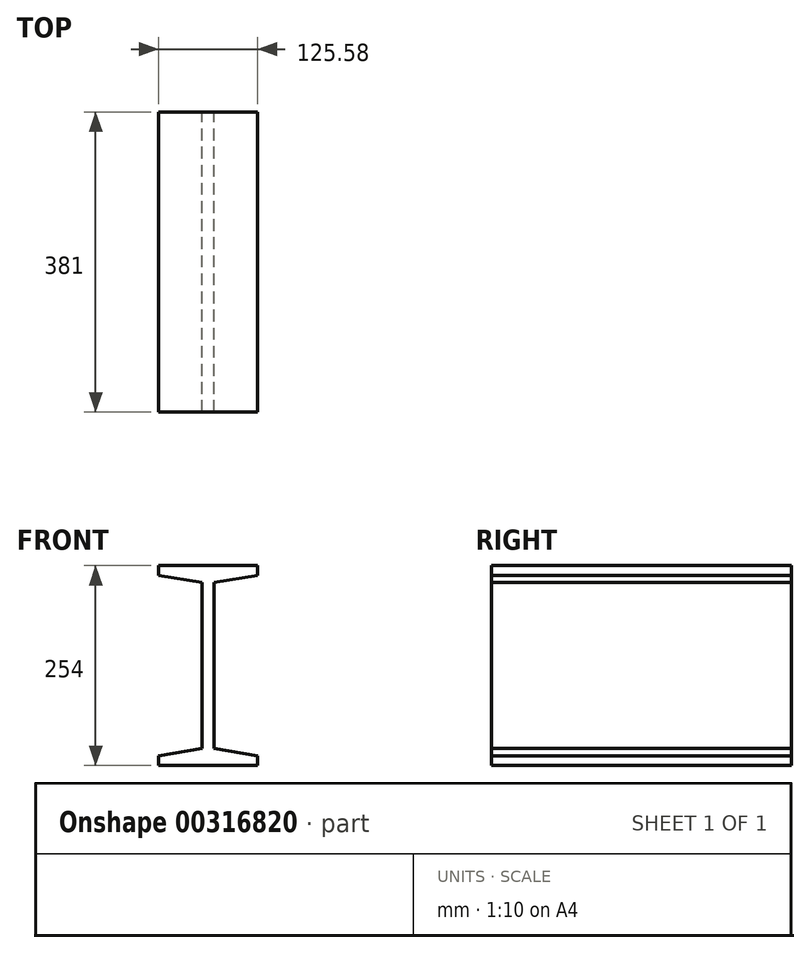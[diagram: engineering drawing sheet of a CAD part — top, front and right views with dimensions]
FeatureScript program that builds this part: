
annotation { "Feature Type Name" : "Feature", "Feature Type Description" : "" }
export const myFeature = defineFeature(function(context is Context, id is Id, definition is map)
    precondition{}
    {
        {
            var Q0;
            Q0=qCreatedBy(makeId("Front.planeOp"),FACE);
            var sketch = newSketch(context, id + "F0", { "sketchPlane" : qUnion([Q0])});
            skLineSegment(sketch, "E0", {"start": v(-62.79, 127) * mm, "end": v(62.79, 127) * mm});
            skLineSegment(sketch, "E1", {"start": v(62.79, 127) * mm, "end": v(62.79, 114.53) * mm});
            skLineSegment(sketch, "E2", {"start": v(-62.79, 127) * mm, "end": v(-62.79, 114.53) * mm});
            skLineSegment(sketch, "E3", {"start": v(-62.79, 114.53) * mm, "end": v(-7.54, 105.32) * mm});
            skLineSegment(sketch, "E4", {"start": v(7.54, 105.32) * mm, "end": v(62.79, 114.53) * mm});
            skLineSegment(sketch, "E5", {"start": v(7.54, 105.32) * mm, "end": v(7.54, -105.32) * mm});
            skLineSegment(sketch, "E6", {"start": v(7.54, -105.32) * mm, "end": v(62.79, -114.53) * mm});
            skLineSegment(sketch, "E7", {"start": v(62.79, -114.53) * mm, "end": v(62.79, -127) * mm});
            skLineSegment(sketch, "E8", {"start": v(62.79, -127) * mm, "end": v(-62.79, -127) * mm});
            skLineSegment(sketch, "E9", {"start": v(-7.54, -105.32) * mm, "end": v(-7.54, 105.32) * mm});
            skLineSegment(sketch, "E10", {"start": v(-62.79, -127) * mm, "end": v(-62.79, -114.53) * mm});
            skLineSegment(sketch, "E11", {"start": v(-62.79, -114.53) * mm, "end": v(-7.54, -105.32) * mm});
            skLineSegment(sketch, "E12", {"start": v(0, 0) * mm, "end": v(135.24, 0) * mm, "construction": true});
            skLineSegment(sketch, "E13", {"start": v(0, 0) * mm, "end": v(0, 89.76) * mm, "construction": true});
            skLineSegment(sketch, "E14.bottom", {"start": v(-62.79, -127) * mm, "end": v(62.79, -127) * mm, "construction": true});
            skLineSegment(sketch, "E14.top", {"start": v(-62.79, 127) * mm, "end": v(62.79, 127) * mm, "construction": true});
            skLineSegment(sketch, "E14.left", {"start": v(-62.79, -127) * mm, "end": v(-62.79, 127) * mm, "construction": true});
            skLineSegment(sketch, "E14.right", {"start": v(62.79, -127) * mm, "end": v(62.79, 127) * mm, "construction": true});
            skLineSegment(sketch, "E15", {"start": v(47.55, -111.99) * mm, "end": v(62.79, -111.99) * mm, "construction": true});
            skLineSegment(sketch, "E16", {"start": v(62.79, -111.99) * mm, "end": v(62.79, -114.53) * mm, "construction": true});
            skSolve(sketch);
        }
        {
            var Q0;
            Q0=makeQuery(id+"F0.imprint","IMPRINT",FACE,{"disambiguationData":[TD([[makeQuery(id+"F0.imprint","IMPRINT",EDGE,{"derivedFrom":sQuery(id+"F0.wireOp",EDGE,"E0")}),-1.0]])]});
            extrude(context, id + "F1", {"entities" : qUnion([Q0]), "depth" : 381 * mm});
        }
    });
